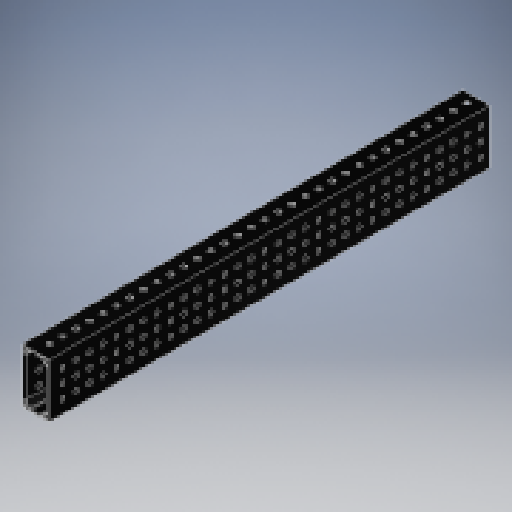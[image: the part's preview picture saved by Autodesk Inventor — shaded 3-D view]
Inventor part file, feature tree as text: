
AUTODESK INVENTOR PART (.ipt)
format: ipt  version: 2024.2 (Build 282272000, 272)  size: 1,084,928 bytes
history: native  units: in
note: dims shown in document units (in); Inventor stores cm internally (conversion verified against a paired STEP export)
features: other x13, extrude x9, hole x3, pattern_linear x3, mirror x3, split x1, sheet_metal_op x1, plane x1, sketch x1
ambient origin geometry x8: Origin, YZ Plane, XZ Plane, XY Plane, X Axis, Y Axis, Z Axis, Center Point
bodies: Solid1 (feature_tree)
feature tree (35):
  other  "MAXTube"
  other  "Blocks"
  other  "Base Sketch"
  extrude  "Base"  Depth=1.0in
  extrude  "MAX Corner"  Depth=0.125in
  extrude  "MAX Corner Cut"  Depth=0.04in
  extrude  "Scribe Lines"  Depth=0.4375in
  other  "Side Middle"
  other  "Top Middle"
  other  "Side Holes Sketch"
  hole  "Top Side Hole"  [1 undecoded]
  hole  "Mid Side Hole"  [1 undecoded]
  hole  "Btm Side Hole"  [1 undecoded]
  pattern_linear  "Side Holes"  Spacing1=0.04in  [1 undecoded]
  mirror  "Side Mirror"
  extrude  "MAXTube Hole"  Depth=1.0in
  extrude  "MAXTube Outside"  TaperAngle=0.0deg  [1 undecoded]
  pattern_linear  "MAXTube Pattern"  Spacing1=17.346in  [1 undecoded]
  mirror  "MAXTube Mirror"
  extrude  "Left Top Hole"  TaperAngle=0.0deg  [1 undecoded]
  extrude  "Mid Top Hole"  TaperAngle=0.0deg  [1 undecoded]
  extrude  "Right Top Hole"  Depth=1.0in
  pattern_linear  "Top Holes"  Spacing1=0.0in  [1 undecoded]
  mirror  "Top Mirror"
  split  "Split1"
  sheet_metal_op  "Corner"
  plane  "Work Plane3"
  sketch  "Sketch5"  dims[d0=2.0in d1=1.0in d2=0.125in d3=0.04in d4=0.4375in d5=0.04in d6=0.0671in d7=0.0272in d8=0.0in d9=0.0in d10=0.0in d11=0.085in d12=0.085in d16=0.04in d17=0.04in d18=0.04in d19=0.04in d20=17.346in d21=0.0in d22=17.346in d23=0.0in d24=0.0in d25=0.0in d26=0.005in d30=0.0in d31=0.0in d34=0.5in d35=0.5in d38=0.5in d40=0.196in d41=0.75in d42=0.375in d43=0.25in d44=0.5635in d45=1.0in d46=0.8108in d47=0.196in d48=0.75in d49=0.375in d50=0.25in d51=0.5635in d52=1.0in d53=0.8108in d54=0.196in d55=0.75in d56=0.375in d57=0.25in d58=0.5635in d59=1.0in d60=0.8108in d61=0.5in d62=6.6929in d64=0.5in d69=1.5in d70=0.0in d71=0.0in d72=1.9685in d74=2.0in d78=2.0in d79=-8.75in d80=0.196in d81=0.0in d82=0.0in d83=0.5in d84=0.0in d85=0.0in d86=0.0in d87=0.0in d88=0.0in d89=0.0in d90=6.6929in d92=0.5in d93=1.0in d95=0.0in d96=0.0in d97=1.846in d98=14.0in d100=-8.75in d101=1.0in]
  other  "Corner:5"
  other  "Corner:6"
  other  "Corner:7"
  other  "Corner:8"
  other  "MAXTube:1"
  other  "MAXTube:2"
  other  "MAXTube:3"
note: 9 required parameter values undecoded (feature->parameter linkage not recoverable at this tier; creation-order binding heuristic only, values carry confidence <= 0.55)
